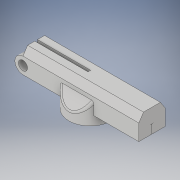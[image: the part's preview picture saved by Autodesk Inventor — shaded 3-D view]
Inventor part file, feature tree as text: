
AUTODESK INVENTOR PART (.ipt)
format: ipt  version: 2019 (Build 230136000, 136)  size: 236,544 bytes
history: native  units: in
note: dims shown in document units (in); Inventor stores cm internally (conversion verified against a paired STEP export)
features: extrude x7, sketch x7, chamfer x2, fillet x2, plane x1
ambient origin geometry x8: Origin, YZ Plane, XZ Plane, XY Plane, X Axis, Y Axis, Z Axis, Center Point
bodies: Solid1 (feature_tree)
feature tree (19):
  extrude  "Extrusion1"  Depth=2.5709in
  extrude  "Extrusion2"  Depth=0.1791in TaperAngle=0.0deg
  extrude  "Extrusion3"  Depth=0.1969in TaperAngle=0.0deg
  chamfer  "Chamfer3"  Distance=0.1969in
  chamfer  "Chamfer4"  Distance=1.378in
  fillet  "Fillet4"  Radius=0.5827in
  fillet  "Fillet5"  Radius=0.2756in
  extrude  "Extrusion6"  Depth=1.1811in TaperAngle=120.0deg
  plane  "Work Plane2"
  extrude  "Extrusion10"  Depth=1.1811in
  extrude  "Extrusion11"  Depth=1.1811in
  extrude  "Extrusion12"  Depth=1.1811in
  sketch  "Sketch1"  dims[d0=0.2008in d2=2.5709in]
  sketch  "Sketch2"  dims[d3=0.1791in d4=0.5827in d5=0.0in]
  sketch  "Sketch3"  dims[d6=0.5118in d7=0.1969in d8=0.0in]
  sketch  "Sketch10"  dims[d9=2.315in]
  sketch  "Sketch14"  dims[d11=0.9449in d13=0.1969in d14=0.0in]
  sketch  "Sketch15"  dims[d15=0.2913in]
  sketch  "Sketch16"  dims[d16=0.2913in d30=1.378in d45=0.5827in d46=0.2756in d47=0.1811in d48=120.0deg d49=0.1811in d50=0.2756in d51=120.0deg d52=0.0787in d53=0.0787in d54=0.8661in d55=0.0394in d56=0.0in d57=0.5827in d58=0.2913in d82=90.0deg d84=0.1181in d85=0.1575in d86=0.1181in d87=1.1811in d88=0.0in d89=1.1811in d90=0.0in d91=1.1811in d92=0.0in]
